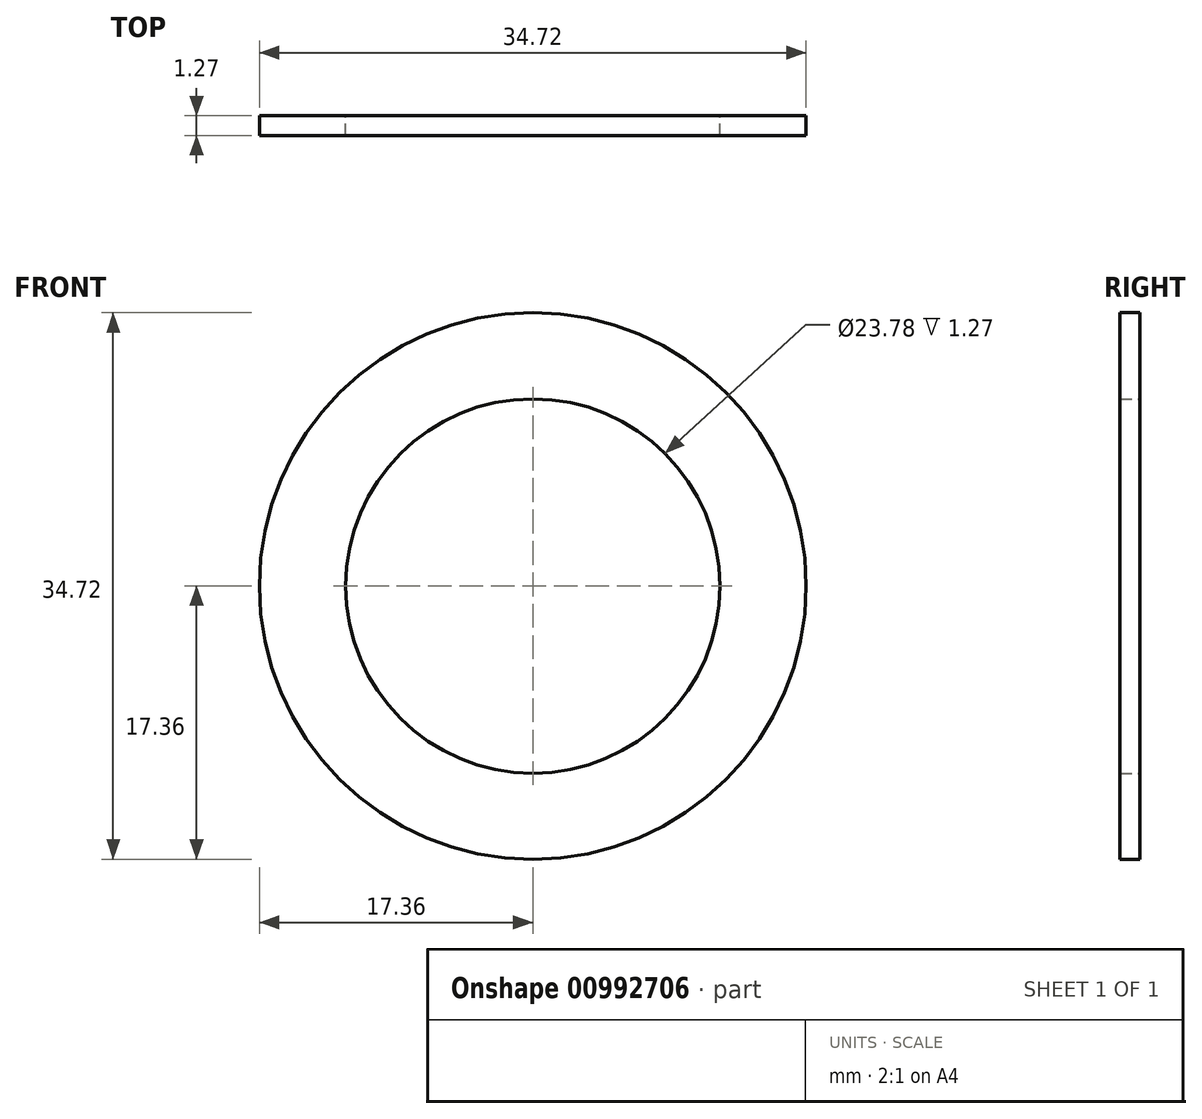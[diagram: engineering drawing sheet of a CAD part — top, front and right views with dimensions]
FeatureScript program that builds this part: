
annotation { "Feature Type Name" : "Feature", "Feature Type Description" : "" }
export const myFeature = defineFeature(function(context is Context, id is Id, definition is map)
    precondition{}
    {
        {
            var Q0;
            Q0=qCreatedBy(makeId("Front.planeOp"),FACE);
            var sketch = newSketch(context, id + "F0", { "sketchPlane" : qUnion([Q0])});
            skCircle(sketch, "E0", {"center": v(0, 0) * mm, "radius": 17.36 * mm});
            skCircle(sketch, "E1", {"center": v(0, 0) * mm, "radius": 11.89 * mm});
            skSolve(sketch);
        }
        {
            var Q0;
            Q0=qSketchRegion(id+"F0",true);
            extrude(context, id + "F1", {"entities" : qUnion([Q0]), "depth" : 1.27 * mm, "offsetDistance" : 25.4 * mm});
        }
    });
